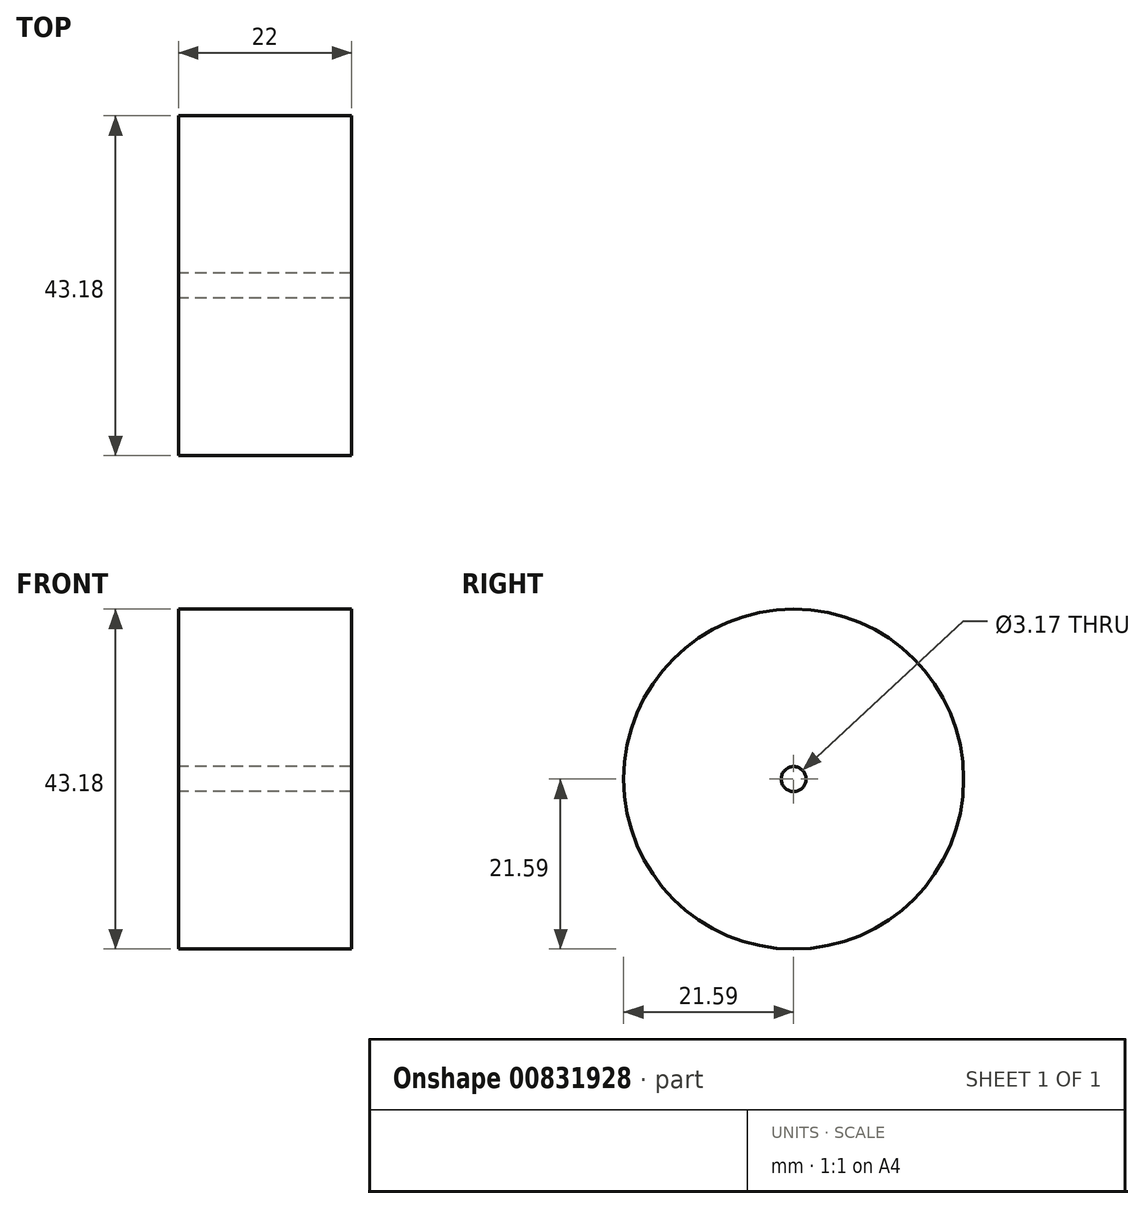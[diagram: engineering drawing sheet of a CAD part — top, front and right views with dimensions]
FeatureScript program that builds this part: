
annotation { "Feature Type Name" : "Feature", "Feature Type Description" : "" }
export const myFeature = defineFeature(function(context is Context, id is Id, definition is map)
    precondition{}
    {
        {
            var Q0;
            Q0=qCreatedBy(makeId("Right.planeOp"),FACE);
            var sketch = newSketch(context, id + "F0", { "sketchPlane" : qUnion([Q0])});
            skCircle(sketch, "E0", {"center": v(0, 0) * mm, "radius": 21.59 * mm});
            skCircle(sketch, "E1", {"center": v(0, 0) * mm, "radius": 1.59 * mm});
            skSolve(sketch);
        }
        {
            var Q0;
            Q0=makeQuery(id+"F0.imprint","IMPRINT",FACE,{"disambiguationData":[TD([[makeQuery(id+"F0.imprint","IMPRINT",EDGE,{"derivedFrom":sQuery(id+"F0.wireOp",EDGE,"E0")}),1.0]])]});
            extrude(context, id + "F1", {"entities" : qUnion([Q0]), "depth" : 22 * mm, "offsetDistance" : 25.4 * mm});
        }
    });
